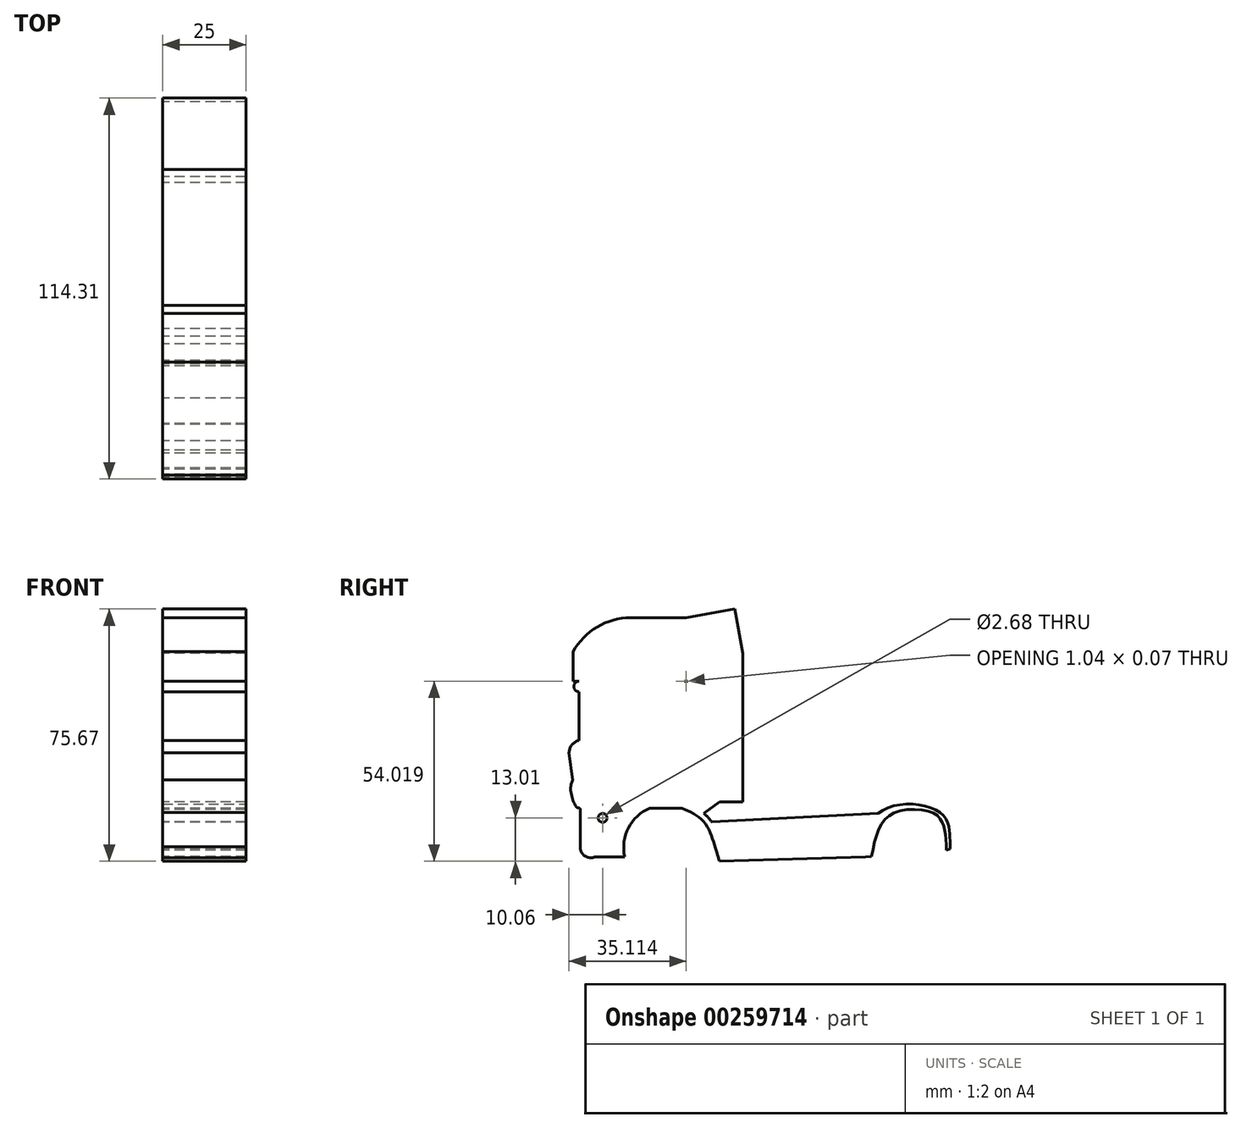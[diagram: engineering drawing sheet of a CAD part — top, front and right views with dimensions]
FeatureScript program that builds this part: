
annotation { "Feature Type Name" : "Feature", "Feature Type Description" : "" }
export const myFeature = defineFeature(function(context is Context, id is Id, definition is map)
    precondition{}
    {
        {
            var Q0;
            Q0=qCreatedBy(makeId("Right.planeOp"),FACE);
            var sketch = newSketch(context, id + "F0", { "sketchPlane" : qUnion([Q0])});
            skLineSegment(sketch, "E0", {"start": v(-43.24, -34.93) * mm, "end": v(-52.1, -34.93) * mm});
            skLineSegment(sketch, "E1", {"start": v(-7.95, 17.73) * mm, "end": v(-58.72, 17.73) * mm});
            skLineSegment(sketch, "E2", {"start": v(-26.03, -20.34) * mm, "end": v(-35.68, -20.34) * mm});
            skLineSegment(sketch, "E3", {"start": v(-26.03, -18.55) * mm, "end": v(-35.68, -18.55) * mm});
            skLineSegment(sketch, "E4", {"start": v(-7.78, -18.51) * mm, "end": v(-14.82, -18.51) * mm});
            skLineSegment(sketch, "E5", {"start": v(-14.82, -18.51) * mm, "end": v(-19.45, -21.9) * mm});
            skPoint(sketch, "E6.end.orphan", {"position": v(-19.45, -31.9) * mm});
            skPoint(sketch, "E6.start.orphan", {"position": v(-19.25, -36.25) * mm});
            skFitSpline(sketch, "E7", {"points": [v(-26.03, -20.34) * mm, v(-19.45, -24.51) * mm, v(-16.12, -31.9) * mm, v(-14.82, -36.25) * mm], "startDerivative": vector(20.45, -9) * mm, "endDerivative": vector(4.29, -14.37) * mm});
            skPoint(sketch, "E8.1.internal.orphan", {"position": v(-54.72, -34.93) * mm});
            skPoint(sketch, "E8.2.internal.orphan", {"position": v(-56.6, -31.9) * mm});
            skLineSegment(sketch, "E9", {"start": v(-58.72, 17.73) * mm, "end": v(-58.72, 26.58) * mm});
            skLineSegment(sketch, "E10", {"start": v(-7.78, -18.51) * mm, "end": v(-7.78, 26.08) * mm});
            skLineSegment(sketch, "E11", {"start": v(-7.78, 26.08) * mm, "end": v(-10.27, 39.42) * mm});
            skLineSegment(sketch, "E12", {"start": v(-10.27, 39.42) * mm, "end": v(-24.86, 36.8) * mm});
            skLineSegment(sketch, "E13", {"start": v(-24.86, 36.8) * mm, "end": v(-41.5, 36.8) * mm});
            skArc(sketch, "E14", {"start": v(-41.5, 36.8) * mm, "mid": v(-51.5, 34.05) * mm, "end": v(-58.72, 26.58) * mm});
            skPoint(sketch, "E15.start.orphan", {"position": v(-35.95, 0) * mm});
            skLineSegment(sketch, "E16", {"start": v(-56.97, 14.61) * mm, "end": v(-56.97, 0) * mm});
            skPoint(sketch, "E17.end.orphan", {"position": v(-35.95, 5.27) * mm});
            skPoint(sketch, "E17.start.orphan", {"position": v(-30.86, -18.55) * mm});
            skLineSegment(sketch, "E18", {"start": v(-33.33, 17.73) * mm, "end": v(-33.33, -14.86) * mm});
            skFitSpline(sketch, "E19", {"points": [v(-20.2, 17.73) * mm, v(-21.36, 26.29) * mm, v(-25.45, 28.62) * mm], "startDerivative": vector(0.34, 17.99) * mm, "endDerivative": vector(-12.56, 3.18) * mm});
            skLineSegment(sketch, "E20", {"start": v(-25.45, 28.62) * mm, "end": v(-25.45, 36.8) * mm});
            skArc(sketch, "E21", {"start": v(-56.6, -31.9) * mm, "mid": v(-55.2, -34.66) * mm, "end": v(-52.1, -34.93) * mm});
            skLineSegment(sketch, "E22", {"start": v(-56.6, -31.9) * mm, "end": v(-56.6, -21.58) * mm});
            skPoint(sketch, "E23.end.orphan", {"position": v(-65.43, 0) * mm});
            skPoint(sketch, "E23.start.orphan", {"position": v(-56.6, -11.07) * mm});
            skArc(sketch, "E24", {"start": v(-56.97, 0) * mm, "mid": v(-59.08, -1.35) * mm, "end": v(-59.94, -3.7) * mm});
            skLineSegment(sketch, "E25", {"start": v(-59.94, -3.7) * mm, "end": v(-58.81, -11.9) * mm});
            skLineSegment(sketch, "E26", {"start": v(-58.81, -1.99) * mm, "end": v(-25.35, 3.7) * mm});
            skLineSegment(sketch, "E27", {"start": v(-25.35, 17.73) * mm, "end": v(-56.97, 17.73) * mm});
            skLineSegment(sketch, "E28", {"start": v(-22.97, 7.07) * mm, "end": v(-22.97, 15.95) * mm});
            skArc(sketch, "E29", {"start": v(-25.35, 3.7) * mm, "mid": v(-23.62, 5) * mm, "end": v(-22.97, 7.07) * mm});
            skArc(sketch, "E30", {"start": v(-22.97, 15.95) * mm, "mid": v(-23.7, 17.43) * mm, "end": v(-25.35, 17.73) * mm});
            skArc(sketch, "E31", {"start": v(-56.97, 17.73) * mm, "mid": v(-58.53, 16.17) * mm, "end": v(-56.97, 14.61) * mm});
            skPoint(sketch, "E32.orphan", {"position": v(52.72, -34.93) * mm});
            skFitSpline(sketch, "E33", {"points": [v(-58.81, -11.9) * mm, v(-59.44, -13.92) * mm, v(-58.81, -17.84) * mm, v(-57.37, -20.2) * mm, v(-56.67, -20.37) * mm, v(-56.6, -21.58) * mm], "startDerivative": vector(-4, -8.8) * mm, "endDerivative": vector(-0.55, -9.9) * mm});
            skPoint(sketch, "E34.1.internal.orphan", {"position": v(-55.19, -20.37) * mm});
            skLineSegment(sketch, "E35", {"start": v(-58.81, -11.9) * mm, "end": v(-56.23, -11.9) * mm});
            skLineSegment(sketch, "E36", {"start": v(-56.23, -11.9) * mm, "end": v(-55.19, -20.37) * mm});
            skLineSegment(sketch, "E37", {"start": v(-55.19, -20.37) * mm, "end": v(-56.67, -20.37) * mm});
            skLineSegment(sketch, "E38", {"start": v(25.05, -32) * mm, "end": v(-14.62, -32) * mm});
            skLineSegment(sketch, "E39", {"start": v(-14.62, -32) * mm, "end": v(-14.62, -29.73) * mm});
            skLineSegment(sketch, "E40", {"start": v(-14.62, -29.73) * mm, "end": v(26.76, -28.81) * mm});
            skLineSegment(sketch, "E41", {"start": v(26.76, -28.81) * mm, "end": v(25.05, -32) * mm});
            skLineSegment(sketch, "E42", {"start": v(-7.7, -29.58) * mm, "end": v(-7.64, -32) * mm});
            skLineSegment(sketch, "E43", {"start": v(-19.5, 17.73) * mm, "end": v(-16.49, -13.35) * mm});
            skLineSegment(sketch, "E44", {"start": v(-18.26, -12.64) * mm, "end": v(-18.26, -5.32) * mm});
            skLineSegment(sketch, "E45", {"start": v(-30.76, -6.52) * mm, "end": v(-31.44, -6.59) * mm});
            skLineSegment(sketch, "E46", {"start": v(-30.81, -13.15) * mm, "end": v(-30.8, -13.35) * mm});
            skLineSegment(sketch, "E47", {"start": v(-18.26, -4.17) * mm, "end": v(-18.56, -0.97) * mm});
            skLineSegment(sketch, "E48", {"start": v(-18.79, -1) * mm, "end": v(-56.02, -4.59) * mm});
            skLineSegment(sketch, "E49", {"start": v(-56.04, -4.7) * mm, "end": v(-59.72, -5.32) * mm});
            skLineSegment(sketch, "E50", {"start": v(-18.26, -4.17) * mm, "end": v(-55.94, -7.8) * mm});
            skPoint(sketch, "E50.endSnap0", {"position": v(-59.38, -7.8) * mm});
            skLineSegment(sketch, "E51", {"start": v(-55.94, -7.8) * mm, "end": v(-59.38, -7.8) * mm});
            skLineSegment(sketch, "E52", {"start": v(-0.4, -26.63) * mm, "end": v(-2.78, -26.63) * mm});
            skLineSegment(sketch, "E53", {"start": v(-0.4, -26.63) * mm, "end": v(-0.46, -25.58) * mm});
            skLineSegment(sketch, "E54", {"start": v(-0.67, -25.6) * mm, "end": v(-2.74, -25.69) * mm});
            skLineSegment(sketch, "E55", {"start": v(-2.75, -25.6) * mm, "end": v(-2.78, -26.63) * mm});
            skPoint(sketch, "E56.end.orphan", {"position": v(-14.82, -24.09) * mm});
            skLineSegment(sketch, "E57", {"start": v(32.9, -21.9) * mm, "end": v(-17.13, -24.42) * mm});
            skArc(sketch, "E58", {"start": v(-14.62, -29.73) * mm, "mid": v(-18.76, -22.54) * mm, "end": v(-26.03, -18.55) * mm});
            skPoint(sketch, "E59.1.internal.orphan", {"position": v(-43.24, -26.59) * mm});
            skPoint(sketch, "E59.2.internal.orphan", {"position": v(-39.07, -20.34) * mm});
            skArc(sketch, "E60", {"start": v(-35.68, -20.34) * mm, "mid": v(-42.12, -26.26) * mm, "end": v(-43.24, -34.93) * mm});
            skArc(sketch, "E61", {"start": v(-35.68, -18.55) * mm, "mid": v(-41.82, -23.28) * mm, "end": v(-43.49, -30.86) * mm});
            skLineSegment(sketch, "E62", {"start": v(-44.17, -27.55) * mm, "end": v(-53.9, -27.55) * mm});
            skLineSegment(sketch, "E63", {"start": v(-42.67, -21.7) * mm, "end": v(-52.17, -21.7) * mm});
            skFitSpline(sketch, "E64", {"points": [v(-52.17, -21.7) * mm, v(-53.2, -21.7) * mm, v(-54, -23.93) * mm, v(-53.9, -27.55) * mm], "startDerivative": vector(-4.62, 1.26) * mm, "endDerivative": vector(0.81, -6.83) * mm});
            skCircle(sketch, "E65", {"center": v(-49.88, -23.24) * mm, "radius": 1.34 * mm});
            skLineSegment(sketch, "E66", {"start": v(-33.33, -10.65) * mm, "end": v(-39.35, -10.65) * mm});
            skLineSegment(sketch, "E67", {"start": v(-33.33, -10.65) * mm, "end": v(-33.33, -6.52) * mm});
            skLineSegment(sketch, "E68", {"start": v(-33.62, -6.47) * mm, "end": v(-36.54, -6.47) * mm});
            skArc(sketch, "E69", {"start": v(-36.54, -6.47) * mm, "mid": v(-38.45, -8.21) * mm, "end": v(-39.35, -10.65) * mm});
            skLineSegment(sketch, "E70", {"start": v(-35.08, -7.61) * mm, "end": v(-35.08, -10.13) * mm});
            skPoint(sketch, "E70.startSnap0", {"position": v(-35.08, -6.47) * mm});
            skLineSegment(sketch, "E71", {"start": v(-35.4, -10.13) * mm, "end": v(-35.4, -7.61) * mm});
            skLineSegment(sketch, "E72", {"start": v(-35.4, -7.61) * mm, "end": v(-35.08, -7.61) * mm});
            skLineSegment(sketch, "E73", {"start": v(-18.26, -12.64) * mm, "end": v(-43.09, -13.64) * mm});
            skPoint(sketch, "E74.end.orphan", {"position": v(-43.81, -12.64) * mm});
            skLineSegment(sketch, "E75", {"start": v(-43.09, -13.64) * mm, "end": v(-44.5, -13.02) * mm});
            skLineSegment(sketch, "E76", {"start": v(-44.5, -13.02) * mm, "end": v(-40.79, -7.81) * mm});
            skLineSegment(sketch, "E77", {"start": v(-40.79, -7.81) * mm, "end": v(-36.54, -6.47) * mm});
            skLineSegment(sketch, "E78", {"start": v(-33.33, -6.52) * mm, "end": v(-30.76, -6.52) * mm});
            skLineSegment(sketch, "E79", {"start": v(-18.26, -5.32) * mm, "end": v(-30.76, -6.52) * mm});
            skLineSegment(sketch, "E80", {"start": v(-30.8, -13.35) * mm, "end": v(-31.44, -6.59) * mm});
            skLineSegment(sketch, "E81", {"start": v(-7.78, -14.07) * mm, "end": v(-38.45, -15.3) * mm});
            skPoint(sketch, "E81.endSnap0", {"position": v(-38.45, -8.21) * mm});
            skLineSegment(sketch, "E82", {"start": v(-38.45, -15.3) * mm, "end": v(-44.01, -19.9) * mm});
            skLineSegment(sketch, "E83", {"start": v(-44.01, -19.9) * mm, "end": v(-55.19, -20.37) * mm});
            skLineSegment(sketch, "E84", {"start": v(-43.5, -30.78) * mm, "end": v(-53.48, -30.78) * mm});
            skLineSegment(sketch, "E85", {"start": v(-53.48, -30.78) * mm, "end": v(-53.9, -27.55) * mm});
            skLineSegment(sketch, "E86", {"start": v(-43.5, -30.78) * mm, "end": v(-44.17, -27.55) * mm});
            skFitSpline(sketch, "E87", {"points": [v(29, -34.93) * mm, v(29, -33.62) * mm, v(32.9, -21.9) * mm, v(51.6, -21.81) * mm, v(54.37, -29.98) * mm, v(54.37, -32.58) * mm, v(54.37, -32.74) * mm], "startDerivative": vector(-2.15, 10.79) * mm, "endDerivative": vector(0.05, -4.12) * mm});
            skLineSegment(sketch, "E88", {"start": v(-14.82, -36.25) * mm, "end": v(29, -34.93) * mm});
            skFitSpline(sketch, "E89", {"points": [v(30.81, -34.83) * mm, v(33.62, -25.44) * mm, v(38.87, -21.26) * mm, v(48.63, -21.47) * mm, v(51.81, -24.07) * mm, v(52.93, -27.57) * mm, v(53.3, -32.87) * mm], "startDerivative": vector(10.27, 49.86) * mm, "endDerivative": vector(1.27, -36.38) * mm});
            skLineSegment(sketch, "E90", {"start": v(30.81, -34.83) * mm, "end": v(29, -34.93) * mm});
            skLineSegment(sketch, "E91", {"start": v(54.37, -32.58) * mm, "end": v(53.3, -32.87) * mm});
            skSolve(sketch);
        }
        {
            var Q0;
            Q0=makeQuery(id+"F0.imprint","IMPRINT",FACE,{"disambiguationData":[TD([[makeQuery(id+"F0.imprint","IMPRINT",EDGE,{"derivedFrom":sQuery(id+"F0.wireOp",EDGE,"E16")}),1.0]])]});
            var Q1;
            {var subQ3=sQuery(id+"F0.wireOp",EDGE,"E9");Q1=makeQuery(id+"F0.imprint","IMPRINT",FACE,{"disambiguationData":[TD([[makeQuery(id+"F0.imprint","IMPRINT",EDGE,{"derivedFrom":subQ3}),-1.0]])]});}
            var Q2;
            {var subQ10=sQuery(id+"F0.wireOp",EDGE,"E28");Q2=makeQuery(id+"F0.imprint","IMPRINT",FACE,{"disambiguationData":[TD([[makeQuery(id+"F0.imprint","IMPRINT",EDGE,{"derivedFrom":subQ10}),1.0]])]});}
            var Q3;
            {var subQ12=sQuery(id+"F0.wireOp",EDGE,"E11");Q3=makeQuery(id+"F0.imprint","IMPRINT",FACE,{"disambiguationData":[TD([[makeQuery(id+"F0.imprint","IMPRINT",EDGE,{"derivedFrom":subQ12}),1.0]])]});}
            var Q4;
            {var subQ2=sQuery(id+"F0.wireOp",EDGE,"E44");Q4=makeQuery(id+"F0.imprint","IMPRINT",FACE,{"disambiguationData":[TD([[makeQuery(id+"F0.imprint","IMPRINT",EDGE,{"derivedFrom":subQ2}),1.0]])]});}
            var Q5;
            {var subQ0=sQuery(id+"F0.wireOp",EDGE,"E66");Q5=makeQuery(id+"F0.imprint","IMPRINT",FACE,{"disambiguationData":[TD([[makeQuery(id+"F0.imprint","IMPRINT",EDGE,{"derivedFrom":subQ0}),1.0]])]});}
            var Q6;
            {var subQ6=sQuery(id+"F0.wireOp",EDGE,"E45");Q6=makeQuery(id+"F0.imprint","IMPRINT",FACE,{"disambiguationData":[TD([[makeQuery(id+"F0.imprint","IMPRINT",EDGE,{"derivedFrom":subQ6}),-1.0]])]});}
            var Q7;
            {var subQ0=sQuery(id+"F0.wireOp",EDGE,"E35");Q7=makeQuery(id+"F0.imprint","IMPRINT",FACE,{"disambiguationData":[TD([[makeQuery(id+"F0.imprint","IMPRINT",EDGE,{"derivedFrom":subQ0}),-1.0]])]});}
            var Q8;
            {var subQ8=sQuery(id+"F0.wireOp",EDGE,"E0");Q8=makeQuery(id+"F0.imprint","IMPRINT",FACE,{"disambiguationData":[TD([[makeQuery(id+"F0.imprint","IMPRINT",EDGE,{"derivedFrom":subQ8}),-1.0]])]});}
            var Q9;
            {var subQ7=sQuery(id+"F0.wireOp",EDGE,"E2");Q9=makeQuery(id+"F0.imprint","IMPRINT",FACE,{"disambiguationData":[TD([[makeQuery(id+"F0.imprint","IMPRINT",EDGE,{"derivedFrom":subQ7}),-1.0]])]});}
            var Q10;
            Q10=makeQuery(id+"F0.imprint","IMPRINT",FACE,{"disambiguationData":[TD([[makeQuery(id+"F0.imprint","IMPRINT",EDGE,{"derivedFrom":sQuery(id+"F0.wireOp",EDGE,"E89")}),1.0]])]});
            var Q11;
            {var subQ0=sQuery(id+"F0.wireOp",EDGE,"E41");Q11=makeQuery(id+"F0.imprint","IMPRINT",FACE,{"disambiguationData":[TD([[makeQuery(id+"F0.imprint","IMPRINT",EDGE,{"derivedFrom":subQ0}),-1.0]])]});}
            var Q12;
            Q12=makeQuery(id+"F0.imprint","IMPRINT",FACE,{"disambiguationData":[TD([[makeQuery(id+"F0.imprint","IMPRINT",EDGE,{"derivedFrom":sQuery(id+"F0.wireOp",EDGE,"E62")}),1.0]])]});
            var Q13;
            {var subQ0=sQuery(id+"F0.wireOp",EDGE,"E39");Q13=makeQuery(id+"F0.imprint","IMPRINT",FACE,{"disambiguationData":[TD([[makeQuery(id+"F0.imprint","IMPRINT",EDGE,{"derivedFrom":subQ0}),-1.0]])]});}
            extrude(context, id + "F1", {"entities" : qUnion([Q0, Q1, Q2, Q3, Q4, Q5, Q6, Q7, Q8, Q9, Q10, Q11, Q12, Q13]), "depth" : 25 * mm, "offsetDistance" : 25 * mm});
        }
    });
